# Revit family: Plumbing-Hot_Water_Heater-Haws_Corporation-Instantaneous_Electric
name_source: partatom
category: Plumbing Fixtures
revit_build: Autodesk Revit 2016 (Build: 20150220_1215(x64)
units: mm (PartAtom-declared; Revit-internal decimal feet)

## family parameters
Always vertical = Yes
Cut with Voids When Loaded = No
OmniClass Number = 23.65.35.11
OmniClass Title = Supply Water Heaters
Part Type = Normal
Room Calculation Point = No
Round Connector Dimension = Use Diameter
Shared = No
Work Plane-Based = No

## types (3) — shared parameters
Description = Instantaneous Electric Water Heater
Design country = USA
Door Thickness = 0' - 1 1/2"
Finish = Metal - Haws Corporation - High Polished Stainless Steel
Manufacturer = Haws Corportation
Piping Clearance Depth = 1' - 6 7/8"
Piping Clearance Length = 6' - 5 25/32"
Tab Offset = 0' - 0 3/4"

## per-type parameters (varying)
| type | Cold Inlet Dist | Depth | Height | Hot Outlet Dist | Input Height | Length | Model | Tab Elevation | Tab Thickness | URL |
| Hawsco_9326 | 1' - 5 7/8" | 1' - 1 1/4" | 2' - 0" | 0' - 5 1/2" | 0' - 6 13/32" | 2' - 6" | 9326 | 0' - 0 15/16" | 0' - 1 31/32" | https://www.hawsco.com |
| Hawsco_9327 | 1' - 5 7/8" | 1' - 1 1/4" | 2' - 0" | 0' - 5 1/2" | 0' - 6 13/32" | 2' - 6" | 9327 | 0' - 0 15/16" | 0' - 1 31/32" | https://www.hawsco.com |
| Hawsco_9321 | 1' - 1 13/32" | 0' - 10 3/8" | 1' - 5 5/8" | 0' - 1 7/16" | 0' - 5 1/4" | 2' - 2 9/32" | 9321 | 0' - 0 9/32" | 0' - 0 7/16" | www.hawsco.com |

## geometry (parser evidence)
native form markers: Blend x22, Sweep x2
no freeform markers — native parametric forms only
